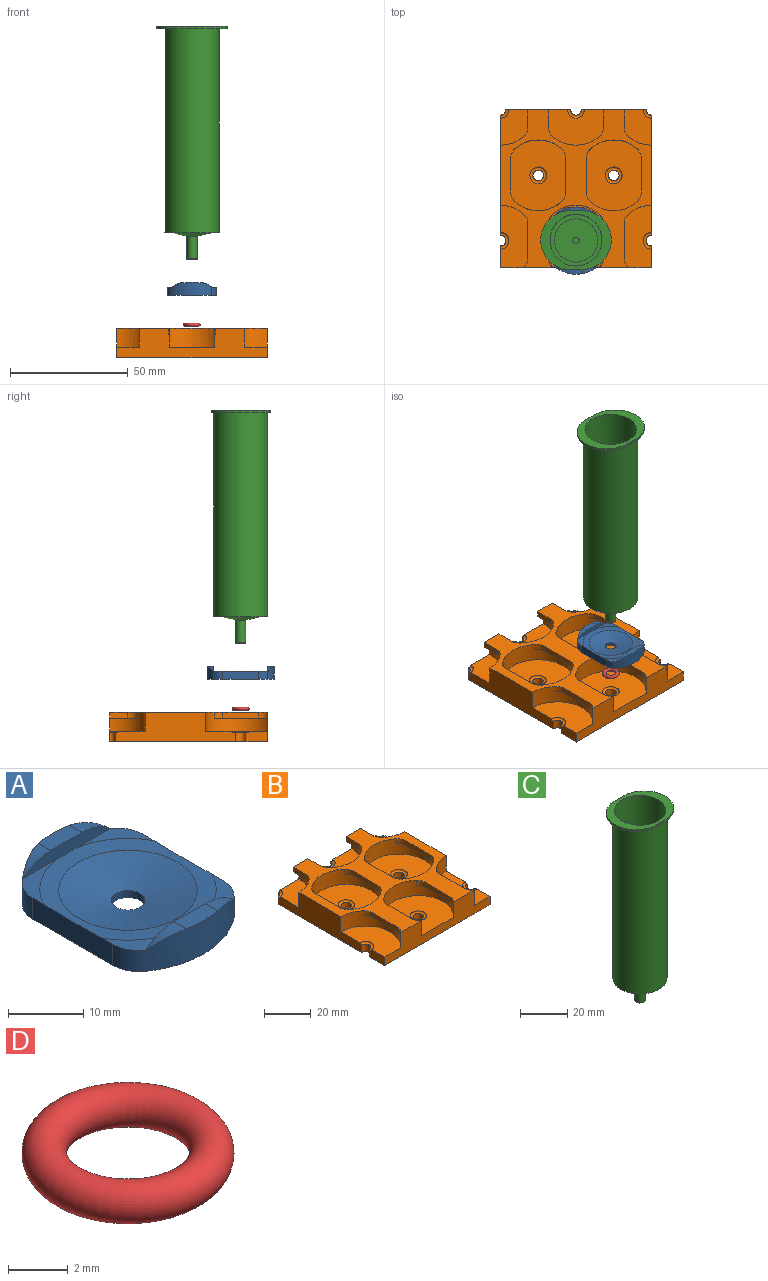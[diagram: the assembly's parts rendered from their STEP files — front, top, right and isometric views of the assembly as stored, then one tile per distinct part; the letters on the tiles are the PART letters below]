
ASSEMBLY  parts=4 mates=3
PART A: 29 faces, bbox 24.2x29.2x6.2 mm
  f0: cylinder r=14.25mm len=16.61mm, axis (0,0,1), area 88.5mm2, adj f2,f7,f8,f9,f12,f15,f22,f23
  f1: cylinder r=14.25mm len=16.61mm, axis (0,0,1), area 88.5mm2, adj f3,f6,f9,f13,f14,f16,f20,f21
  f2: plane 5.92x2.64mm, normal (0,0,1), area 15mm2, adj f0,f4,f26,f27
  f3: plane 5.92x2.64mm, normal (0,0,1), area 15mm2, adj f1,f5,f24,f25
  f4: plane 16.81x2.29mm, normal (0,-1,0), area 26.4mm2, adj f2,f7,f8,f19,f22,f23,f26,f27
  f5: plane 16.81x2.29mm, normal (0,1,0), area 26.4mm2, adj f3,f6,f16,f19,f20,f21,f24,f25
  f6: plane 8.57x6.13mm, normal (0,0,1), area 14.8mm2, adj f1,f5,f10,f13,f19
  f7: plane 8.57x6.13mm, normal (0,0,1), area 14.8mm2, adj f0,f4,f10,f12,f19
  f8: plane 8.57x6.13mm, normal (0,0,1), area 14.8mm2, adj f0,f4,f11,f15,f19
  f9: plane 28.5x20.78mm, normal (0,0,-1), area 491.7mm2, adj f0,f1,f10,f11,f12,f13,f14,f15
  f10: plane 15.03x3.44mm, normal (-1,0,0), area 51.1mm2, adj f6,f7,f9,f12,f13,f19
  f11: plane 15.76x4.17mm, normal (1,0,0), area 51.1mm2, adj f8,f9,f14,f15,f16,f19
  f12: cylinder r=5mm len=4.06mm, axis (0,0,1), area 16.3mm2, adj f0,f7,f9,f10
  f13: cylinder r=5mm len=4.06mm, axis (0,0,1), area 16.3mm2, adj f1,f6,f9,f10
  f14: cylinder r=5mm len=4.06mm, axis (0,0,1), area 16.3mm2, adj f1,f9,f11,f16
  f15: cylinder r=5mm len=4.06mm, axis (0,0,1), area 16.3mm2, adj f0,f8,f9,f11
  f16: plane 8.57x6.13mm, normal (0,0,1), area 14.8mm2, adj f1,f5,f11,f14,f19
  f17: torus R=2.81mm, axis (0,0,1), area 34.4mm2, adj f9,f18
  f18: cylinder r=2.25mm len=4.5mm, axis (0,0,1), area 16.1mm2, adj f17,f28
  f19: cone r=2.25mm half-angle=86.4deg, axis (0,0,1), area 148.5mm2, adj f4,f5,f6,f7,f8,f10,f11,f16
  f20: plane 0.31x0.25mm, normal (-0.62,0,0.78), area 0mm2, adj f1,f5,f25
  f21: plane 0.31x0.25mm, normal (0.62,0,0.78), area 0mm2, adj f1,f5,f24
  f22: plane 0.31x0.25mm, normal (-0.62,0,0.78), area 0mm2, adj f0,f4,f26
  f23: plane 0.31x0.25mm, normal (0.62,0,0.78), area 0mm2, adj f0,f4,f27
  f24: cylinder r=8mm len=5mm, axis (0,-1,0), area 7.7mm2, adj f1,f3,f5,f21
  f25: cylinder r=8mm len=5mm, axis (0,1,0), area 7.7mm2, adj f1,f3,f5,f20
  f26: cylinder r=8mm len=5mm, axis (0,1,0), area 7.7mm2, adj f0,f2,f4,f22
  f27: cylinder r=8mm len=5mm, axis (0,-1,0), area 7.7mm2, adj f0,f2,f4,f23
  f28: cone r=2.25mm half-angle=76.8deg, axis (0,0,1), area 259mm2, adj f18,f19
PART B: 85 faces, bbox 64x67x12.5 mm
  f0: plane 67x64mm, normal (0,0,1), area 1297.2mm2, adj f2,f3,f4,f5,f13,f14,f15,f16
  f1: plane 67x64mm, normal (0,0,-1), area 4208.5mm2, adj f9,f10,f22,f23,f24,f25,f26,f27
  f2: cylinder r=15mm len=15mm, axis (0,0,1), area 156.7mm2, adj f0,f6,f76,f77,f78,f80
  f3: cylinder r=15mm len=26.5mm, axis (0,0,1), area 229.7mm2, adj f0,f7,f55,f64,f65,f80,f82
  f4: cylinder r=15mm len=30mm, axis (0,0,1), area 459.3mm2, adj f0,f8,f39,f41,f50,f51,f52,f53
  f5: cylinder r=15mm len=26.5mm, axis (0,0,1), area 229.7mm2, adj f0,f18,f35,f36,f37,f81,f82
  f6: plane 15x15mm, normal (0,0,1), area 166.7mm2, adj f2,f12,f78,f80
  f7: plane 26.5x15mm, normal (0,0,1), area 310.4mm2, adj f3,f11,f80,f82,f83
  f8: plane 30x26.5mm, normal (0,0,1), area 620.9mm2, adj f4,f29,f82
  f9: cylinder r=2.25mm len=4mm, axis (0,0,1), area 14.2mm2, adj f1,f12,f78,f80
  f10: cylinder r=2.25mm len=4.5mm, axis (0,0,1), area 28.3mm2, adj f1,f11,f80,f83
  f11: torus R=2.81mm, axis (0,0,1), area 17.2mm2, adj f7,f10,f80,f83
  f12: torus R=2.81mm, axis (0,0,1), area 8.6mm2, adj f6,f9,f78,f80
  f13: cylinder r=15mm len=30mm, axis (0,0,1), area 313.3mm2, adj f0,f20,f70,f72,f73,f74,f78,f79
  f14: cylinder r=15mm len=15mm, axis (0,0,1), area 156.7mm2, adj f0,f17,f67,f68,f79,f81
  f15: cylinder r=15mm len=30mm, axis (0,0,1), area 626.6mm2, adj f0,f21,f57,f59,f60,f61,f62,f63
  f16: cylinder r=15mm len=30mm, axis (0,0,1), area 626.6mm2, adj f0,f19,f43,f45,f46,f47,f48,f49
  f17: plane 15x15mm, normal (0,0,1), area 166.7mm2, adj f14,f32,f79,f81
  f18: plane 26.5x15mm, normal (0,0,1), area 310.4mm2, adj f5,f28,f81,f82,f84
  f19: plane 30x30mm, normal (0,0,1), area 667mm2, adj f16,f30
  f20: plane 30x15mm, normal (0,0,1), area 333.5mm2, adj f13,f33,f78,f79
  f21: plane 30x30mm, normal (0,0,1), area 667mm2, adj f15,f31
  f22: cylinder r=2.25mm len=4mm, axis (0,0,1), area 14.2mm2, adj f1,f32,f79,f81
  f23: cylinder r=2.25mm len=4.5mm, axis (0,0,1), area 56.6mm2, adj f1,f30
  f24: cylinder r=2.25mm len=4.5mm, axis (0,0,1), area 56.6mm2, adj f1,f29
  f25: cylinder r=2.25mm len=4.5mm, axis (0,0,1), area 28.3mm2, adj f1,f28,f81,f84
  f26: cylinder r=2.25mm len=4.5mm, axis (0,0,1), area 28.3mm2, adj f1,f33,f78,f79
  f27: cylinder r=2.25mm len=4.5mm, axis (0,0,1), area 56.6mm2, adj f1,f31
  f28: torus R=2.81mm, axis (0,0,1), area 17.2mm2, adj f18,f25,f81,f84
  f29: torus R=2.81mm, axis (0,0,1), area 34.4mm2, adj f8,f24
  f30: torus R=2.81mm, axis (0,0,1), area 34.4mm2, adj f19,f23
  f31: torus R=2.81mm, axis (0,0,1), area 34.4mm2, adj f21,f27
  f32: torus R=2.81mm, axis (0,0,1), area 8.6mm2, adj f17,f22,f79,f81
  f33: torus R=2.81mm, axis (0,0,1), area 17.2mm2, adj f20,f26,f78,f79
  f34: plane 15.01x2.5mm, normal (1,0,0), area 37.5mm2, adj f0,f35,f36,f37
  f35: plane 22.52x5.09mm, normal (0,0,-1), area 45.1mm2, adj f5,f34,f36,f37
  f36: cylinder r=5mm len=3.75mm, axis (0,0,1), area 10.6mm2, adj f0,f5,f34,f35
  f37: cylinder r=5mm len=3.75mm, axis (0,0,1), area 10.6mm2, adj f0,f5,f34,f35
  f38: plane 15.01x2.5mm, normal (1,0,0), area 37.5mm2, adj f0,f39,f52,f53
  f39: plane 22.52x5.09mm, normal (0,0,-1), area 45.1mm2, adj f4,f38,f52,f53
  f40: plane 15.01x2.5mm, normal (-1,0,0), area 37.5mm2, adj f0,f41,f50,f51
  f41: plane 22.52x5.09mm, normal (0,0,-1), area 45.1mm2, adj f4,f40,f50,f51
  f42: plane 15.01x2.5mm, normal (1,0,0), area 37.5mm2, adj f0,f43,f48,f49
  f43: plane 22.52x5.09mm, normal (0,0,-1), area 45.1mm2, adj f16,f42,f48,f49
  f44: plane 15.01x2.5mm, normal (-1,0,0), area 37.5mm2, adj f0,f45,f46,f47
  f45: plane 22.52x5.09mm, normal (0,0,-1), area 45.1mm2, adj f16,f44,f46,f47
  f46: cylinder r=5mm len=3.75mm, axis (0,0,1), area 10.6mm2, adj f0,f16,f44,f45
  f47: cylinder r=5mm len=3.75mm, axis (0,0,1), area 10.6mm2, adj f0,f16,f44,f45
  f48: cylinder r=5mm len=3.75mm, axis (0,0,1), area 10.6mm2, adj f0,f16,f42,f43
  f49: cylinder r=5mm len=3.75mm, axis (0,0,1), area 10.6mm2, adj f0,f16,f42,f43
  f50: cylinder r=5mm len=3.75mm, axis (0,0,1), area 10.6mm2, adj f0,f4,f40,f41
  f51: cylinder r=5mm len=3.75mm, axis (0,0,1), area 10.6mm2, adj f0,f4,f40,f41
  f52: cylinder r=5mm len=3.75mm, axis (0,0,1), area 10.6mm2, adj f0,f4,f38,f39
  f53: cylinder r=5mm len=3.75mm, axis (0,0,1), area 10.6mm2, adj f0,f4,f38,f39
  f54: plane 15.01x2.5mm, normal (-1,0,0), area 37.5mm2, adj f0,f55,f64,f65
  f55: plane 22.52x5.09mm, normal (0,0,-1), area 45.1mm2, adj f3,f54,f64,f65
  f56: plane 15.01x2.5mm, normal (1,0,0), area 37.5mm2, adj f0,f57,f62,f63
  f57: plane 22.52x5.09mm, normal (0,0,-1), area 45.1mm2, adj f15,f56,f62,f63
  f58: plane 15.01x2.5mm, normal (-1,0,0), area 37.5mm2, adj f0,f59,f60,f61
  f59: plane 22.52x5.09mm, normal (0,0,-1), area 45.1mm2, adj f15,f58,f60,f61
  f60: cylinder r=5mm len=3.75mm, axis (0,0,1), area 10.6mm2, adj f0,f15,f58,f59
  f61: cylinder r=5mm len=3.75mm, axis (0,0,1), area 10.6mm2, adj f0,f15,f58,f59
  f62: cylinder r=5mm len=3.75mm, axis (0,0,1), area 10.6mm2, adj f0,f15,f56,f57
  f63: cylinder r=5mm len=3.75mm, axis (0,0,1), area 10.6mm2, adj f0,f15,f56,f57
  f64: cylinder r=5mm len=3.75mm, axis (0,0,1), area 10.6mm2, adj f0,f3,f54,f55
  f65: cylinder r=5mm len=3.75mm, axis (0,0,1), area 10.6mm2, adj f0,f3,f54,f55
  f66: plane 7.51x2.5mm, normal (1,0,0), area 18.8mm2, adj f0,f67,f68,f79
  f67: plane 11.26x5.09mm, normal (0,0,-1), area 22.6mm2, adj f14,f66,f68,f79
  f68: cylinder r=5mm len=3.75mm, axis (0,0,1), area 10.6mm2, adj f0,f14,f66,f67
  f69: plane 7.51x2.5mm, normal (1,0,0), area 18.8mm2, adj f0,f70,f74,f78
  f70: plane 11.26x5.09mm, normal (0,0,-1), area 22.6mm2, adj f13,f69,f74,f78
  f71: plane 7.51x2.5mm, normal (-1,0,0), area 18.8mm2, adj f0,f72,f73,f79
  f72: plane 11.26x5.09mm, normal (0,0,-1), area 22.6mm2, adj f13,f71,f73,f79
  f73: cylinder r=5mm len=3.75mm, axis (0,0,1), area 10.6mm2, adj f0,f13,f71,f72
  f74: cylinder r=5mm len=3.75mm, axis (0,0,1), area 10.6mm2, adj f0,f13,f69,f70
  f75: plane 7.51x2.5mm, normal (-1,0,0), area 18.8mm2, adj f0,f76,f77,f78
  f76: plane 11.26x5.09mm, normal (0,0,-1), area 22.6mm2, adj f2,f75,f77,f78
  f77: cylinder r=5mm len=3.75mm, axis (0,0,1), area 10.6mm2, adj f0,f2,f75,f76
  f78: plane 27.5x12.5mm, normal (0,1,0), area 155.1mm2, adj f0,f1,f2,f6,f9,f12,f13,f20
  f79: plane 27.5x12.5mm, normal (0,1,0), area 155.1mm2, adj f0,f1,f13,f14,f17,f20,f22,f26
  f80: plane 51x12.5mm, normal (-1,0,0), area 431.9mm2, adj f0,f1,f2,f3,f6,f7,f9,f10
  f81: plane 51x12.5mm, normal (1,0,0), area 431.9mm2, adj f0,f1,f5,f14,f17,f18,f22,f25
  f82: plane 64x12.5mm, normal (0,-1,0), area 491.8mm2, adj f0,f1,f3,f4,f5,f7,f8,f18
  f83: plane 9.25x4.5mm, normal (-1,0,0), area 40.8mm2, adj f1,f7,f10,f11,f82
  f84: plane 9.25x4.5mm, normal (1,0,0), area 40.8mm2, adj f1,f18,f25,f28,f82
PART C: 16 faces, bbox 30x25x99 mm
  f0: cylinder r=11mm len=87mm, axis (0,0,-1), area 6013mm2, adj f1,f2
  f1: plane 30x25mm, normal (0,0,1), area 235.7mm2, adj f0,f3,f4,f5,f6
  f2: plane 22x22mm, normal (0,0,1), area 380.1mm2, adj f0
  f3: plane 5x1mm, normal (0,1,0), area 5mm2, adj f1,f4,f6,f7
  f4: cylinder r=12.5mm len=25mm, axis (0,0,1), area 39.3mm2, adj f1,f3,f5,f7
  f5: plane 5x1mm, normal (0,-1,0), area 5mm2, adj f1,f4,f6,f7
  f6: cylinder r=12.5mm len=25mm, axis (0,0,1), area 39.3mm2, adj f1,f3,f5,f7
  f7: plane 30x25mm, normal (0,0,-1), area 200.4mm2, adj f3,f4,f5,f6,f9
  f8: plane 23x23mm, normal (0,0,-1), area 149.6mm2, adj f9,f15
  f9: cylinder r=11.5mm len=86.5mm, axis (0,0,-1), area 6250.2mm2, adj f7,f8
  f10: cylinder r=1.4mm len=11.5mm, axis (0,0,1), area 101.2mm2, adj f12,f13
  f11: cylinder r=2.2mm len=9.6mm, axis (0,0,1), area 132.7mm2, adj f14,f15
  f12: plane 3.6x3.6mm, normal (0,0,-1), area 4mm2, adj f10,f14
  f13: plane 2.8x2.8mm, normal (0,0,-1), area 6.2mm2, adj f10
  f14: torus R=1.8mm, axis (0,0,-1), area 8.1mm2, adj f11,f12
  f15: cone r=2.2mm half-angle=77.9deg, axis (0,0,1), area 256.4mm2, adj f8,f11
PART D: 1 faces, bbox 7.7x7.7x1.5 mm
  f0: torus R=2.81mm, axis (0,0,-1), area 83.3mm2
PLACE A t=(589.91,97.97,29.55)mm
PLACE B t=(385.91,87.47,10.11)mm
PLACE C t=(7.91,-9.53,59.25)mm
PLACE D t=(481.91,87.47,19.61)mm
MATE fastened C.f11 <-> A.f0  axis (0,0,1) through (7.91,-9.53,58.75)mm
MATE fastened A.f0 <-> B.f4  axis (0,0,-1) through (7.91,-9.53,32.11)mm
MATE fastened D.f0 <-> A.f0  axis (0,0,-1) through (7.91,-9.53,19.61)mm
